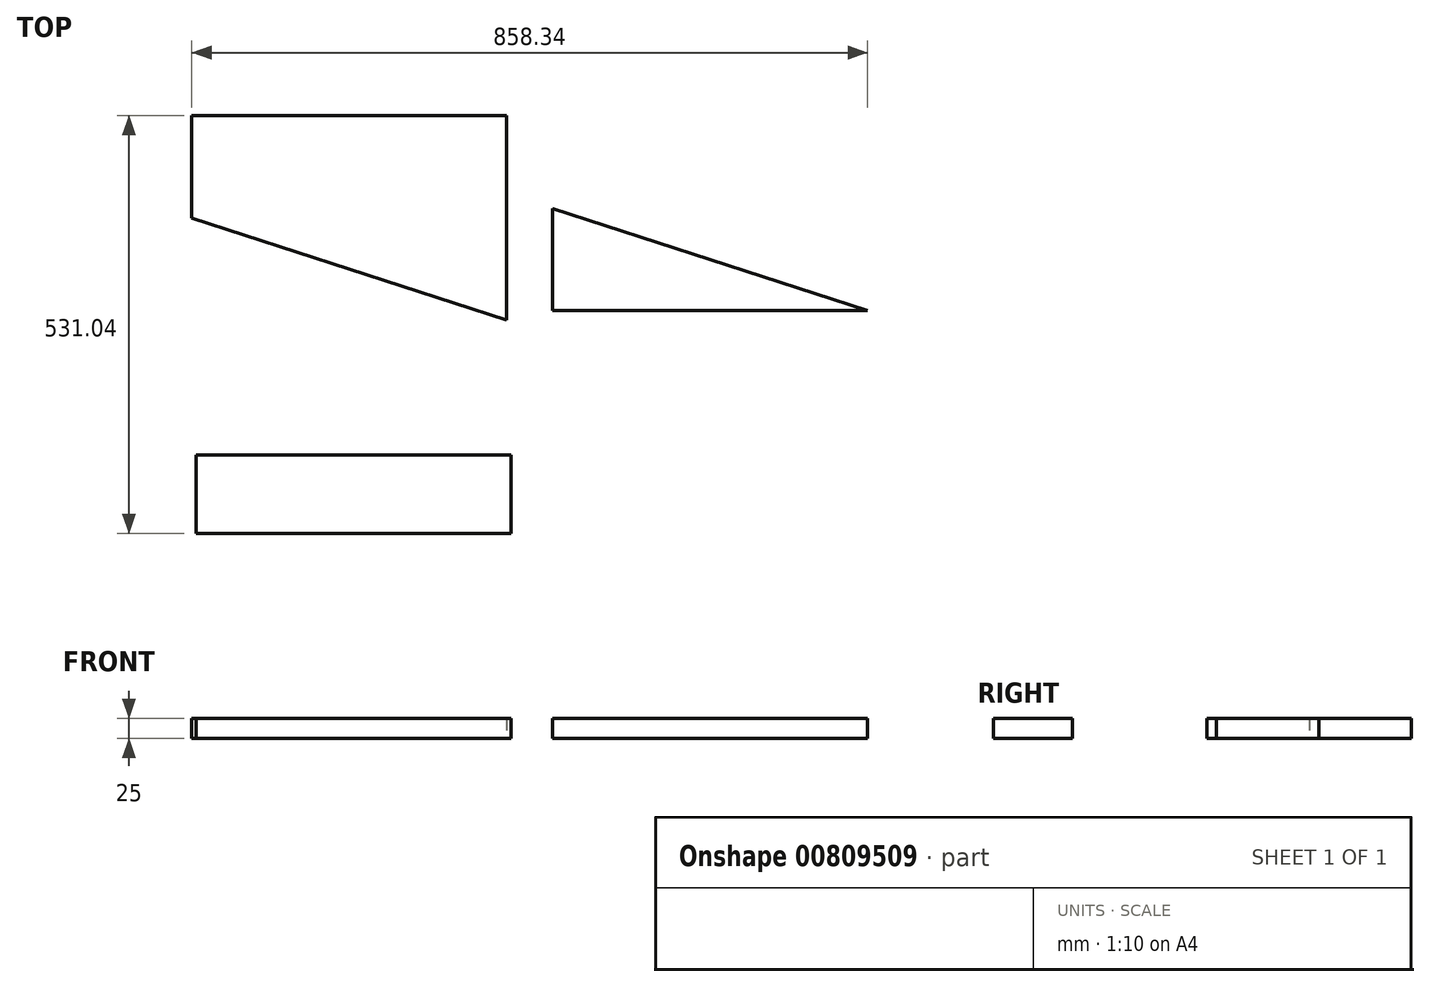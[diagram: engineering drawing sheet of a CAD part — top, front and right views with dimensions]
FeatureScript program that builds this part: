
annotation { "Feature Type Name" : "Feature", "Feature Type Description" : "" }
export const myFeature = defineFeature(function(context is Context, id is Id, definition is map)
    precondition{}
    {
        {
            var Q0;
            Q0=qCreatedBy(makeId("Top.planeOp"),FACE);
            var sketch = newSketch(context, id + "F0", { "sketchPlane" : qUnion([Q0])});
            skLineSegment(sketch, "E0.bottom", {"start": v(-302.37, -215.92) * mm, "end": v(97.63, -215.92) * mm});
            skLineSegment(sketch, "E0.top", {"start": v(-302.37, -315.92) * mm, "end": v(97.63, -315.92) * mm});
            skLineSegment(sketch, "E0.left", {"start": v(-302.37, -215.92) * mm, "end": v(-302.37, -315.92) * mm});
            skLineSegment(sketch, "E0.right", {"start": v(97.63, -215.92) * mm, "end": v(97.63, -315.92) * mm});
            skLineSegment(sketch, "E1.bottom", {"start": v(-307.87, 215.12) * mm, "end": v(92.13, 215.12) * mm});
            skLineSegment(sketch, "E1.left", {"start": v(-307.87, 215.12) * mm, "end": v(-307.87, 85.12) * mm});
            skLineSegment(sketch, "E1.right", {"start": v(92.13, 215.12) * mm, "end": v(92.13, -44.88) * mm});
            skLineSegment(sketch, "E2.top", {"start": v(150.47, -32.76) * mm, "end": v(550.47, -32.76) * mm});
            skLineSegment(sketch, "E2.left", {"start": v(150.47, 97.24) * mm, "end": v(150.47, -32.76) * mm});
            skLineSegment(sketch, "E3", {"start": v(-307.87, 85.12) * mm, "end": v(92.13, -44.88) * mm});
            skLineSegment(sketch, "E4", {"start": v(150.47, 97.24) * mm, "end": v(150.47, 97.24) * mm});
            skLineSegment(sketch, "E5", {"start": v(92.13, -44.88) * mm, "end": v(92.13, -44.88) * mm});
            skLineSegment(sketch, "E6", {"start": v(150.47, 97.24) * mm, "end": v(550.47, -32.76) * mm});
            skLineSegment(sketch, "E7", {"start": v(550.47, -32.76) * mm, "end": v(550.47, -32.76) * mm});
            skSolve(sketch);
        }
        {
            var Q0;
            Q0 = qSketchRegion(id + "F0", true);
            extrude(context, id + "F1", {"entities" : qUnion([Q0]), "depth" : 25 * mm, "offsetDistance" : 25 * mm});
        }
    });
